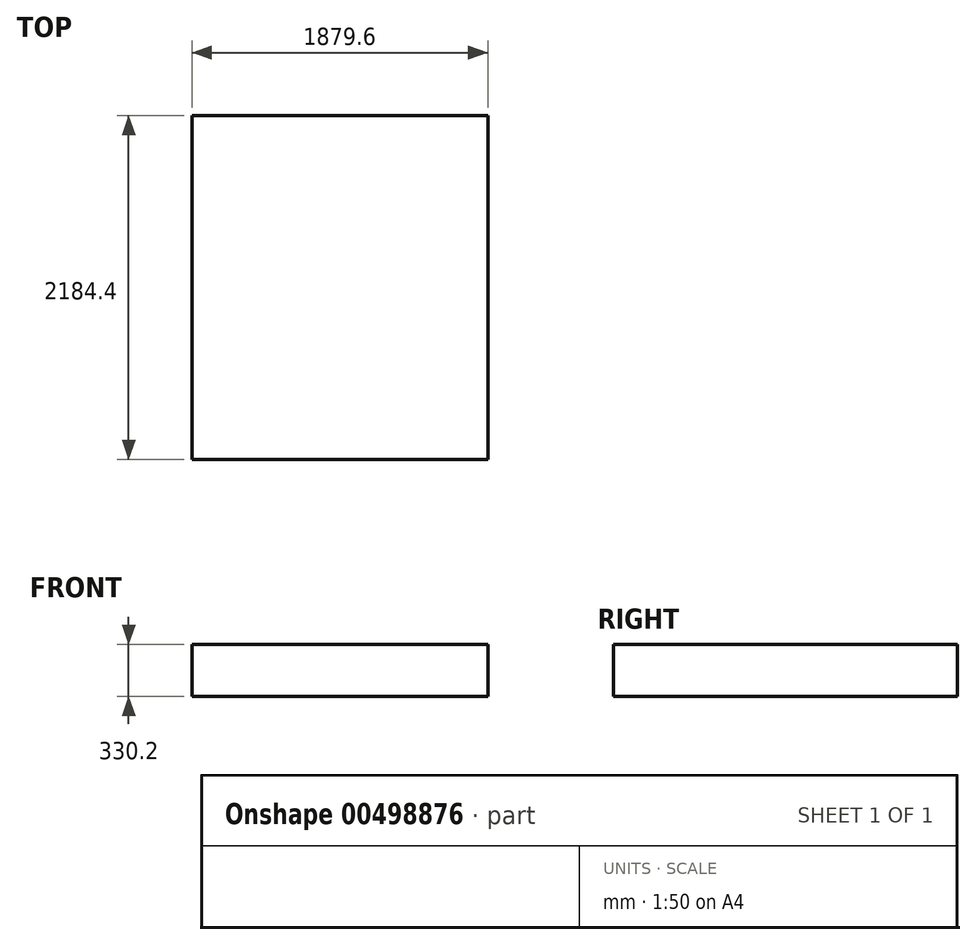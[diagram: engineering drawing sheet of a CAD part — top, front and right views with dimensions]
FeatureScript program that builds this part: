
annotation { "Feature Type Name" : "Feature", "Feature Type Description" : "" }
export const myFeature = defineFeature(function(context is Context, id is Id, definition is map)
    precondition{}
    {
        {
            var Q0;
            Q0=qCreatedBy(makeId("Top.planeOp"),FACE);
            var sketch = newSketch(context, id + "F0", { "sketchPlane" : qUnion([Q0])});
            skLineSegment(sketch, "E0.bottom", {"start": v(-833.98, 1180.28) * mm, "end": v(1045.62, 1180.28) * mm});
            skLineSegment(sketch, "E0.top", {"start": v(-833.98, -1004.12) * mm, "end": v(1045.62, -1004.12) * mm});
            skLineSegment(sketch, "E0.left", {"start": v(-833.98, 1180.28) * mm, "end": v(-833.98, -1004.12) * mm});
            skLineSegment(sketch, "E0.right", {"start": v(1045.62, 1180.28) * mm, "end": v(1045.62, -1004.12) * mm});
            skSolve(sketch);
        }
        {
            var Q0;
            Q0=makeQuery(id+"F0.imprint","IMPRINT",FACE,{"disambiguationData":[TD([[makeQuery(id+"F0.imprint","IMPRINT",EDGE,{"derivedFrom":sQuery(id+"F0.wireOp",EDGE,"E0.bottom")}),-1.0]])]});
            extrude(context, id + "F1", {"entities" : qUnion([Q0]), "depth" : 330.2 * mm});
        }
    });
